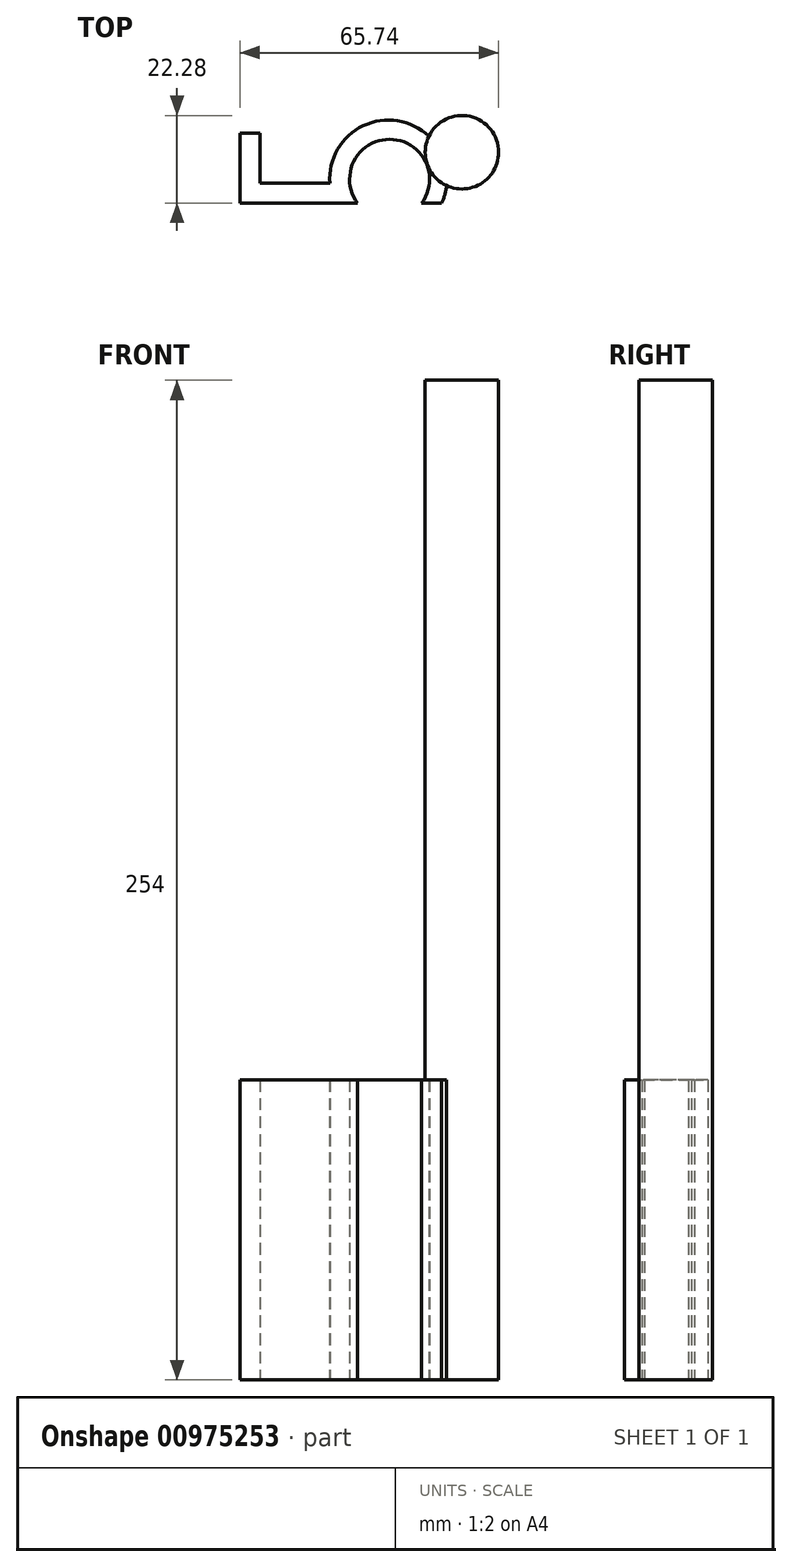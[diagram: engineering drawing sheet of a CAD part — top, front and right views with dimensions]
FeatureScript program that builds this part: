
annotation { "Feature Type Name" : "Feature", "Feature Type Description" : "" }
export const myFeature = defineFeature(function(context is Context, id is Id, definition is map)
    precondition{}
    {
        {
            var Q0;
            Q0=qCreatedBy(makeId("Top.planeOp"),FACE);
            var sketch = newSketch(context, id + "F0", { "sketchPlane" : qUnion([Q0])});
            skLineSegment(sketch, "E0", {"start": v(-46.17, 30.23) * mm, "end": v(-41.09, 30.23) * mm});
            skLineSegment(sketch, "E1", {"start": v(-46.17, 30.23) * mm, "end": v(-46.17, 12.45) * mm});
            skLineSegment(sketch, "E2", {"start": v(-41.09, 30.23) * mm, "end": v(-41.09, 17.53) * mm});
            skLineSegment(sketch, "E3", {"start": v(-41.09, 17.53) * mm, "end": v(-23.3, 17.53) * mm});
            skLineSegment(sketch, "E4", {"start": v(-46.17, 12.45) * mm, "end": v(-16.29, 12.45) * mm});
            skArc(sketch, "E5", {"start": v(0, 12.45) * mm, "mid": v(-8.14, 28.68) * mm, "end": v(-16.29, 12.45) * mm});
            skArc(sketch, "E6", {"start": v(5.08, 12.45) * mm, "mid": v(-5.83, 33.33) * mm, "end": v(-23.3, 17.53) * mm});
            skLineSegment(sketch, "E7", {"start": v(0, 12.45) * mm, "end": v(5.08, 12.45) * mm});
            skSolve(sketch);
        }
        {
            var Q0;
            Q0=makeQuery(id+"F0.imprint","IMPRINT",FACE,{"disambiguationData":[TD([[makeQuery(id+"F0.imprint","IMPRINT",EDGE,{"derivedFrom":sQuery(id+"F0.wireOp",EDGE,"E0")}),-1.0]])]});
            extrude(context, id + "F1", {"entities" : qUnion([Q0]), "depth" : 76.2 * mm, "offsetDistance" : 25.4 * mm});
        }
        {
            var Q0;
            Q0=qCreatedBy(makeId("Top.planeOp"),FACE);
            var sketch = newSketch(context, id + "F2", { "sketchPlane" : qUnion([Q0])});
            skCircle(sketch, "E8", {"center": v(10.23, 25.4) * mm, "radius": 9.33 * mm});
            skSolve(sketch);
        }
        {
            var Q0;
            Q0 = qSketchRegion(id + "F2", true);
            extrude(context, id + "F3", {"entities" : qUnion([Q0]), "operationType" : NewBodyOperationType.ADD, "depth" : 254 * mm, "offsetDistance" : 25.4 * mm});
        }
    });
